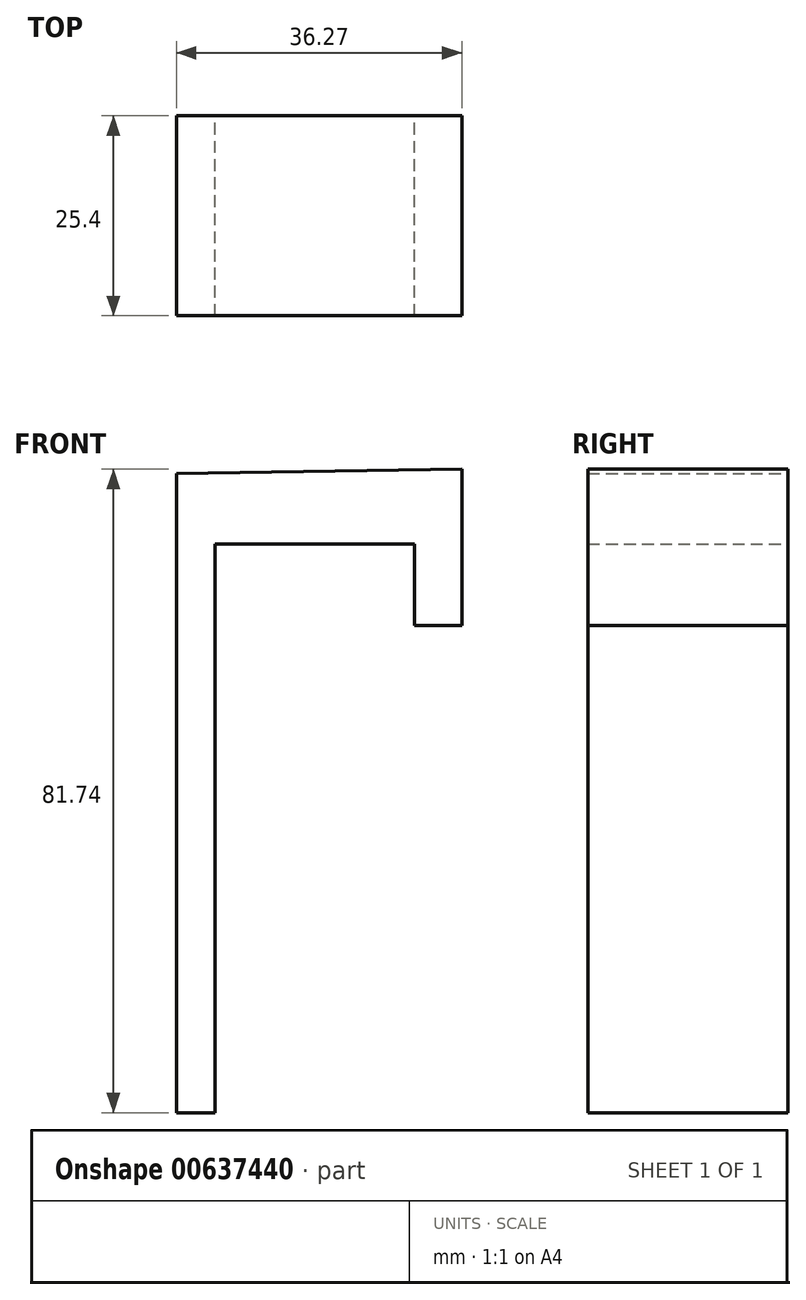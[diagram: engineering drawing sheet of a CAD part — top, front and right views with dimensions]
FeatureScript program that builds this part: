
annotation { "Feature Type Name" : "Feature", "Feature Type Description" : "" }
export const myFeature = defineFeature(function(context is Context, id is Id, definition is map)
    precondition{}
    {
        {
            var Q0;
            Q0=qCreatedBy(makeId("Front.planeOp"),FACE);
            var sketch = newSketch(context, id + "F0", { "sketchPlane" : qUnion([Q0])});
            skLineSegment(sketch, "E0", {"start": v(-62.6, 41.88) * mm, "end": v(-62.6, -39.29) * mm});
            skLineSegment(sketch, "E1", {"start": v(-62.6, -39.29) * mm, "end": v(-57.7, -39.29) * mm});
            skLineSegment(sketch, "E2", {"start": v(-57.7, -39.29) * mm, "end": v(-57.7, 32.95) * mm});
            skLineSegment(sketch, "E3", {"start": v(-57.7, 32.95) * mm, "end": v(-32.38, 32.95) * mm});
            skLineSegment(sketch, "E4", {"start": v(-32.38, 32.95) * mm, "end": v(-32.38, 22.6) * mm});
            skLineSegment(sketch, "E5", {"start": v(-32.38, 22.6) * mm, "end": v(-26.33, 22.6) * mm});
            skLineSegment(sketch, "E6", {"start": v(-26.33, 22.6) * mm, "end": v(-26.33, 42.45) * mm});
            skLineSegment(sketch, "E7", {"start": v(-26.33, 42.45) * mm, "end": v(-62.6, 41.88) * mm});
            skSolve(sketch);
        }
        {
            var Q0;
            Q0 = qSketchRegion(id + "F0", true);
            extrude(context, id + "F1", {"entities" : qUnion([Q0]), "depth" : 25.4 * mm, "offsetDistance" : 25.4 * mm});
        }
    });
